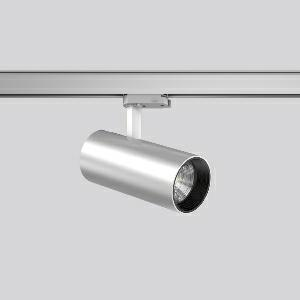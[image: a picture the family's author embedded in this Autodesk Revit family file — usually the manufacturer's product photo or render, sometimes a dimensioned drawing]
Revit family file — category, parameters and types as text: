
# Revit family: deecos_s_mini_742194_004_1_76_c0e9
name_source: partatom
category: Lighting Fixtures
units: mm (PartAtom-declared; Revit-internal decimal feet)

## family parameters
Cut with Voids When Loaded = No
Host = Face
Light Source = No
Part Type = Normal
Room Calculation Point = No
Round Connector Dimension = Use Diameter
Shared = No

## types (1)
- DEECOS S mini (1 x LED Modul 940, 2250 lm, 4000)
    Apparent Load = 22 VA
    Approval mark = CE
    CIE Flux Codes = 99 100 100 100 100
    Color Rendering = 92
    Color Temperature = 4000
    Default Elevation = 1800 mm
    Description = Series: DEECOS S mini
LED surface-mounted projector in modern design with no visible cooling ribs. Housing: die-cast aluminium, powder-coated. Rotation range: 356°. Swivel range: 90°. Black plastic ring and recessed LED to prevent glare from the side. Optical assembly with lens made of plastic (polycarbonate) for the best homogeneous light distribution - can be changed without tools. Best colour rendering index Ra>90. Superspot version with small spot LED. With adapter for RZB 3-circuit DALI tracks. Suitable for Track on ceiling, Wall track. High quality converter without flickering and stroboscopic effect. The following accessories can be mounted without use of tools: interchangeable lenses, decorative glasses, honeycomb louvre, clear and frosted diffusers, white interchangeable plastic ring. 
Colour: silver
Diameter: 87 mm
Height: 214 mm
Lamp: LED
Socket: without socket
Colour temperature: 4000K
Colour rendering index (CRI): 92
System power: 22 W
Rated luminous flux: 2250 lm
Luminous efficiency: 102 lm/W
Control gear: Converter, dimmable, DALI
Protection class: I
Type of protection: IP 20
    Height = 214 mm
    Lamp = 1 x LED Modul 940
    Lamp Light Flux = 2250 lm
    Lamp count = 1
    Length = 87 mm
    Lifetime = 50000 h
    Luminous efficacy = 102 lm/W
    Manufacturer = RZB
    ModVariant = No
    Model = 742194.004.1.76
    Mounting Place = Ceiling
    Mounting Type = Rail mounted
    Number of Poles = 1
    OnlyDefault = Yes
    Power Factor = 1
    Product Name = DEECOS S mini
    Product group = Track mounted projectors
    ProductGroupID = 301
    Protection Class = Protection class I
    Protection Degree = IP 20
    RLX_Detail_Level = 1
    RLX_Emergency_Light_Flux = 0 lm
    RLX_Emergency_Type = 0
    RLX_Emergency_Type_DB = No
    RlxData = <blob elided: 37505 chars, md5=78a13b35>
    Socket = socket
    Standby Power = 0 W
    System Light Flux = 2250 lm
    System Power = 22 W
    Type Comments = Product without accessories
    Type Image = 741930.004.jpg
    URL = http://relux.com
    VarID = ---
    Voltage = 230 V
    Voltage Range = 220-240 V
    Weight = 0.00 kg
    Width = 0 mm  [stored 0 ft]

note: [stored X ft] marks values corroborated as IEEE doubles in the binary element streams (Revit-internal decimal feet)

## geometry (parser evidence)
native form markers: Blend x4, Sweep x13
no freeform markers — native parametric forms only
